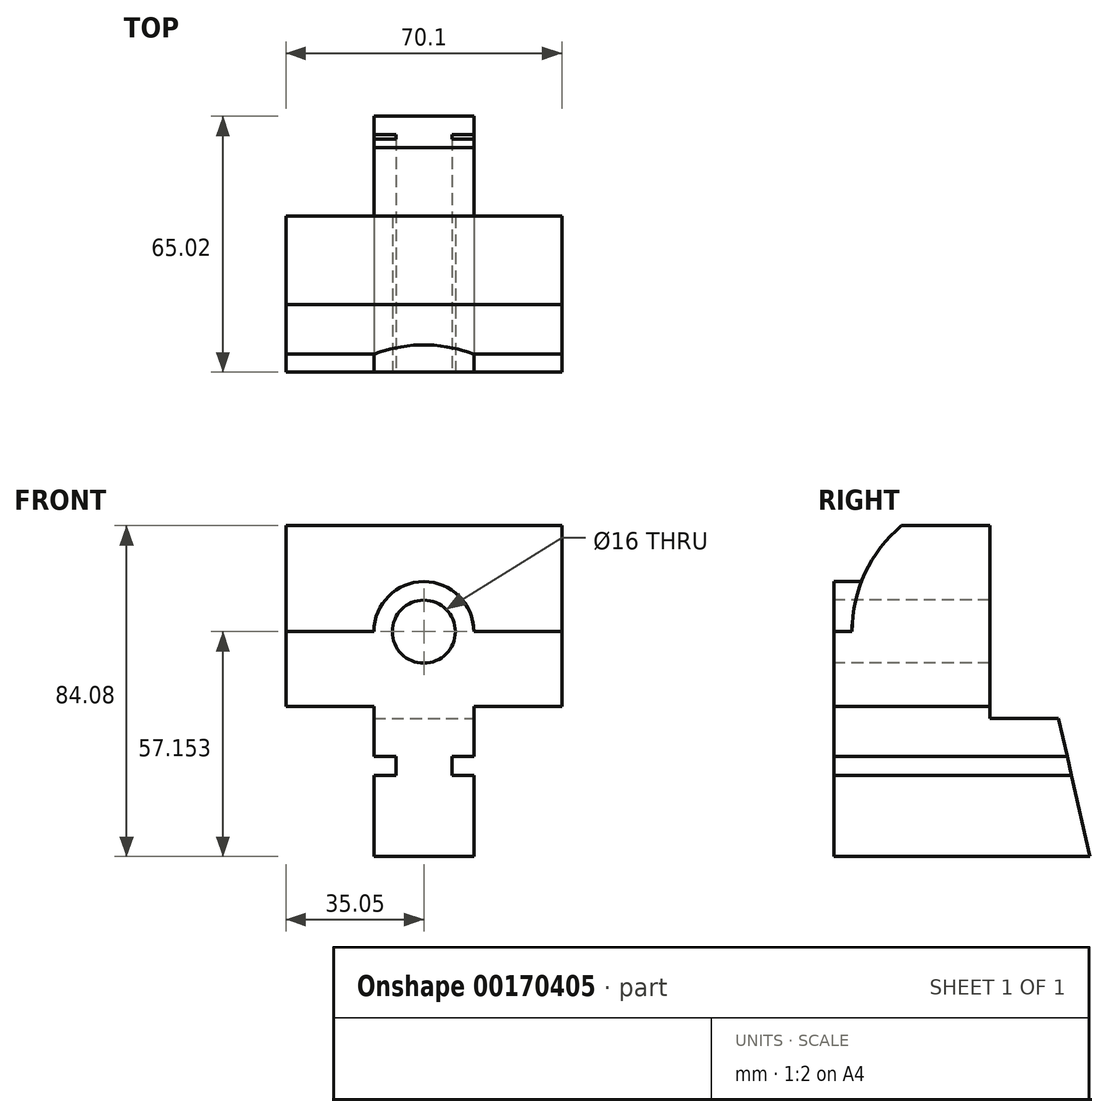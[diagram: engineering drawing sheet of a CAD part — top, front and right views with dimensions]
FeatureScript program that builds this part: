
annotation { "Feature Type Name" : "Feature", "Feature Type Description" : "" }
export const myFeature = defineFeature(function(context is Context, id is Id, definition is map)
    precondition{}
    {
        {
            var Q0;
            Q0=qCreatedBy(makeId("Right.planeOp"),FACE);
            var sketch = newSketch(context, id + "F0", { "sketchPlane" : qUnion([Q0])});
            skLineSegment(sketch, "E0.bottom", {"start": v(-32.51, 42.04) * mm, "end": v(32.51, 42.04) * mm});
            skLineSegment(sketch, "E0.top", {"start": v(-32.51, -42.04) * mm, "end": v(32.51, -42.04) * mm});
            skLineSegment(sketch, "E0.left", {"start": v(-32.51, 42.04) * mm, "end": v(-32.51, -42.04) * mm});
            skLineSegment(sketch, "E0.right", {"start": v(32.51, 42.04) * mm, "end": v(32.51, -42.04) * mm});
            skPoint(sketch, "E0.middle", {"position": v(0, 0) * mm});
            skSolve(sketch);
        }
        {
            var Q0;
            Q0 = qSketchRegion(id + "F0", true);
            extrude(context, id + "F1", {"entities" : qUnion([Q0]), "endBound" : BoundingType.SYMMETRIC, "depth" : 70.1 * mm});
        }
        {
            var Q0;
            Q0=qCreatedBy(makeId("Front.planeOp"),FACE);
            var sketch = newSketch(context, id + "F2", { "sketchPlane" : qUnion([Q0])});
            skLineSegment(sketch, "E1.bottom", {"start": v(-44.45, -3.94) * mm, "end": v(-12.7, -3.94) * mm});
            skLineSegment(sketch, "E1.top", {"start": v(-44.45, -67.44) * mm, "end": v(-12.7, -67.44) * mm});
            skLineSegment(sketch, "E1.left", {"start": v(-44.45, -3.94) * mm, "end": v(-44.45, -67.44) * mm});
            skLineSegment(sketch, "E1.right", {"start": v(-12.7, -3.94) * mm, "end": v(-12.7, -16.64) * mm});
            skLineSegment(sketch, "E2", {"start": v(-12.7, -3.94) * mm, "end": v(12.7, -3.94) * mm, "construction": true});
            skLineSegment(sketch, "E3.bottom", {"start": v(12.7, -3.94) * mm, "end": v(44.45, -3.94) * mm});
            skLineSegment(sketch, "E3.top", {"start": v(12.7, -67.44) * mm, "end": v(44.45, -67.44) * mm});
            skLineSegment(sketch, "E3.left", {"start": v(12.7, -3.94) * mm, "end": v(12.7, -16.64) * mm});
            skLineSegment(sketch, "E3.right", {"start": v(44.45, -3.94) * mm, "end": v(44.45, -67.44) * mm});
            skLineSegment(sketch, "E4", {"start": v(-12.7, -16.64) * mm, "end": v(-7.11, -16.64) * mm});
            skLineSegment(sketch, "E5", {"start": v(-7.11, -16.64) * mm, "end": v(-7.11, -21.46) * mm});
            skLineSegment(sketch, "E6", {"start": v(-7.11, -21.46) * mm, "end": v(-12.7, -21.46) * mm});
            skLineSegment(sketch, "E7.trimOffspring", {"start": v(-12.7, -21.46) * mm, "end": v(-12.7, -67.44) * mm});
            skLineSegment(sketch, "E8.MirrorCS", {"start": v(12.7, -16.64) * mm, "end": v(7.11, -16.64) * mm});
            skLineSegment(sketch, "E9.MirrorCS", {"start": v(7.11, -16.64) * mm, "end": v(7.11, -21.46) * mm});
            skLineSegment(sketch, "E10.MirrorCS", {"start": v(7.11, -21.46) * mm, "end": v(12.7, -21.46) * mm});
            skLineSegment(sketch, "E11.trimOffspring", {"start": v(12.7, -21.46) * mm, "end": v(12.7, -67.44) * mm});
            skSolve(sketch);
        }
        {
            var Q0;
            Q0 = qSketchRegion(id + "F2", true);
            extrude(context, id + "F3", {"entities" : qUnion([Q0]), "operationType" : NewBodyOperationType.REMOVE, "endBound" : BoundingType.SYMMETRIC, "oppositeDirection" : true, "depth" : 254 * mm});
        }
        {
            var Q0;
            Q0=qCreatedBy(makeId("Right.planeOp"),FACE);
            var sketch = newSketch(context, id + "F4", { "sketchPlane" : qUnion([Q0])});
            skLineSegment(sketch, "E12.bottom", {"start": v(7.11, 52.99) * mm, "end": v(79.57, 52.99) * mm});
            skLineSegment(sketch, "E12.top", {"start": v(7.11, -6.99) * mm, "end": v(79.57, -6.99) * mm});
            skLineSegment(sketch, "E12.left", {"start": v(7.11, 52.99) * mm, "end": v(7.11, -6.99) * mm});
            skLineSegment(sketch, "E12.right", {"start": v(79.57, 52.99) * mm, "end": v(79.57, -6.99) * mm});
            skSolve(sketch);
        }
        {
            var Q0;
            Q0 = qSketchRegion(id + "F4", true);
            extrude(context, id + "F5", {"entities" : qUnion([Q0]), "operationType" : NewBodyOperationType.REMOVE, "endBound" : BoundingType.SYMMETRIC, "oppositeDirection" : true, "depth" : 254 * mm});
        }
        {
            var Q0;
            Q0=makeQuery(id+"F3.boolean.opBoolean","COPY",FACE,{"derivedFrom":makeQuery(id+"F3.opExtrude","SWEPT_FACE",FACE,{"disambiguationData":[OSD([sQuery(id+"F2.wireOp",EDGE,"E11.trimOffspring")])]})});
            var sketch = newSketch(context, id + "F6", { "sketchPlane" : qUnion([Q0])});
            skLineSegment(sketch, "E13", {"start": v(32.51, -42.04) * mm, "end": v(22.86, 0.47) * mm});
            skLineSegment(sketch, "E14", {"start": v(22.86, 0.47) * mm, "end": v(55.86, 0.47) * mm});
            skLineSegment(sketch, "E15", {"start": v(55.86, 0.47) * mm, "end": v(52.07, -65.31) * mm});
            skLineSegment(sketch, "E16", {"start": v(52.07, -65.31) * mm, "end": v(32.51, -42.04) * mm});
            skSolve(sketch);
        }
        {
            var Q0;
            Q0 = qSketchRegion(id + "F6", true);
            extrude(context, id + "F7", {"entities" : qUnion([Q0]), "operationType" : NewBodyOperationType.REMOVE, "endBound" : BoundingType.SYMMETRIC, "oppositeDirection" : true, "depth" : 254 * mm});
        }
        {
            var Q0;
            Q0=qCreatedBy(makeId("Right.planeOp"),FACE);
            var sketch = newSketch(context, id + "F8", { "sketchPlane" : qUnion([Q0])});
            skArc(sketch, "E17", {"start": v(7.2, 50.16) * mm, "mid": v(-17.61, 39.96) * mm, "end": v(-27.94, 15.19) * mm});
            skLineSegment(sketch, "E18", {"start": v(7.2, 50.16) * mm, "end": v(-34.92, 66.14) * mm});
            skLineSegment(sketch, "E19", {"start": v(-34.92, 66.14) * mm, "end": v(-47.84, 20.21) * mm});
            skLineSegment(sketch, "E20", {"start": v(-47.84, 20.21) * mm, "end": v(-47.84, 15.19) * mm});
            skLineSegment(sketch, "E21", {"start": v(-47.84, 15.19) * mm, "end": v(-27.94, 15.19) * mm});
            skSolve(sketch);
        }
        {
            var Q0;
            Q0 = qSketchRegion(id + "F8", true);
            extrude(context, id + "F9", {"entities" : qUnion([Q0]), "operationType" : NewBodyOperationType.REMOVE, "endBound" : BoundingType.SYMMETRIC, "oppositeDirection" : true, "depth" : 254 * mm});
        }
        {
            var Q0;
            Q0=makeQuery(id+"F1.opExtrude","SWEPT_FACE",FACE,{"disambiguationData":[OSD([sQuery(id+"F0.wireOp",EDGE,"E0.left")])]});
            var sketch = newSketch(context, id + "F10", { "sketchPlane" : qUnion([Q0])});
            skCircle(sketch, "E22", {"center": v(0, 15.11) * mm, "radius": 12.7 * mm});
            skSolve(sketch);
        }
        {
            var Q0;
            Q0 = qSketchRegion(id + "F10", true);
            extrude(context, id + "F11", {"entities" : qUnion([Q0]), "operationType" : NewBodyOperationType.ADD, "oppositeDirection" : true, "depth" : 25.4 * mm});
        }
        {
            var Q0;
            Q0=makeQuery(id+"F11.boolean.opBoolean","MERGE",FACE,{"derivedFrom":[makeQuery(id+"F1.opExtrude","SWEPT_FACE",FACE,{"disambiguationData":[OSD([sQuery(id+"F0.wireOp",EDGE,"E0.left")])]}),makeQuery(id+"F11.opExtrude","CAP_FACE",FACE,{"disambiguationData":[OSD([sQuery(id+"F10.wireOp",EDGE,"E22")])],"isStart":true})]});
            var sketch = newSketch(context, id + "F12", { "sketchPlane" : qUnion([Q0])});
            skCircle(sketch, "E23", {"center": v(0, 15.11) * mm, "radius": 8 * mm});
            skSolve(sketch);
        }
        {
            var Q0;
            Q0 = qSketchRegion(id + "F12", true);
            extrude(context, id + "F13", {"entities" : qUnion([Q0]), "operationType" : NewBodyOperationType.REMOVE, "endBound" : BoundingType.THROUGH_ALL, "oppositeDirection" : true, "depth" : 25.4 * mm});
        }
    });
